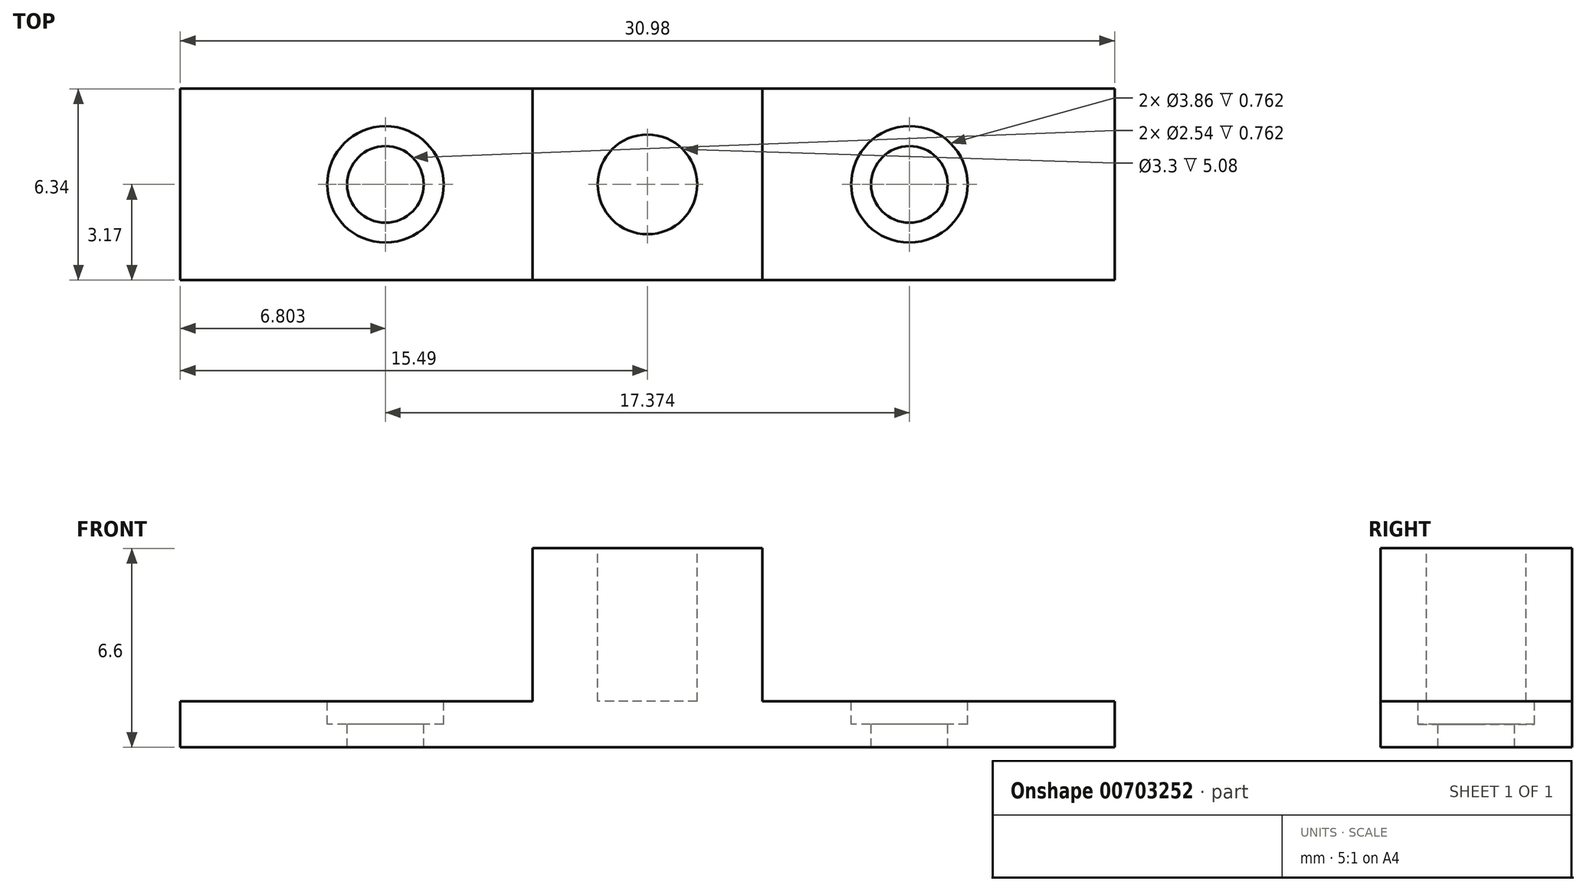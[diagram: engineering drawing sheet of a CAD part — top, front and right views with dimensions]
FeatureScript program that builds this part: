
annotation { "Feature Type Name" : "Feature", "Feature Type Description" : "" }
export const myFeature = defineFeature(function(context is Context, id is Id, definition is map)
    precondition{}
    {
        {
            var Q0;
            Q0=qCreatedBy(makeId("Top.planeOp"),FACE);
            var sketch = newSketch(context, id + "F0", { "sketchPlane" : qUnion([Q0])});
            skLineSegment(sketch, "E0", {"start": v(-15.5, 3.17) * mm, "end": v(15.5, 3.17) * mm});
            skLineSegment(sketch, "E1", {"start": v(15.5, 3.17) * mm, "end": v(15.5, -3.17) * mm});
            skLineSegment(sketch, "E2", {"start": v(15.5, -3.17) * mm, "end": v(-15.5, -3.18) * mm});
            skLineSegment(sketch, "E3", {"start": v(-15.5, -3.18) * mm, "end": v(-15.5, 3.17) * mm});
            skSolve(sketch);
        }
        {
            var Q0;
            Q0=makeQuery(id+"F0.imprint","IMPRINT",FACE,{"disambiguationData":[TD([[makeQuery(id+"F0.imprint","IMPRINT",EDGE,{"derivedFrom":sQuery(id+"F0.wireOp",EDGE,"E0")}),-1.0]])]});
            extrude(context, id + "F1", {"entities" : qUnion([Q0]), "depth" : 1.52 * mm, "offsetDistance" : 25.4 * mm});
        }
        {
            var Q0;
            Q0=makeQuery(id+"F1.opExtrude","CAP_FACE",FACE,{"disambiguationData":[OSD([sQuery(id+"F0.wireOp",EDGE,"E0"),sQuery(id+"F0.wireOp",EDGE,"E1"),sQuery(id+"F0.wireOp",EDGE,"E2"),sQuery(id+"F0.wireOp",EDGE,"E3")])],"isStart":false});
            var sketch = newSketch(context, id + "F2", { "sketchPlane" : qUnion([Q0])});
            skCircle(sketch, "E4", {"center": v(-8.69, 0) * mm, "radius": 1.93 * mm});
            skCircle(sketch, "E5", {"center": v(8.69, 0) * mm, "radius": 1.93 * mm});
            skSolve(sketch);
        }
        {
            var Q0;
            Q0 = qSketchRegion(id + "F2", true);
            extrude(context, id + "F3", {"entities" : qUnion([Q0]), "operationType" : NewBodyOperationType.REMOVE, "oppositeDirection" : true, "depth" : 0.76 * mm, "offsetDistance" : 25.4 * mm});
        }
        {
            var Q0;
            Q0=makeQuery(id+"F3.boolean.opBoolean","COPY",FACE,{"derivedFrom":makeQuery(id+"F3.opExtrude","CAP_FACE",FACE,{"disambiguationData":[OSD([sQuery(id+"F2.wireOp",EDGE,"E4")])],"isStart":false})});
            var sketch = newSketch(context, id + "F4", { "sketchPlane" : qUnion([Q0])});
            skCircle(sketch, "E6", {"center": v(-8.69, 0) * mm, "radius": 1.27 * mm});
            skCircle(sketch, "E7", {"center": v(8.69, 0) * mm, "radius": 1.27 * mm});
            skSolve(sketch);
        }
        {
            var Q0;
            Q0 = qSketchRegion(id + "F4", true);
            extrude(context, id + "F5", {"entities" : qUnion([Q0]), "operationType" : NewBodyOperationType.REMOVE, "oppositeDirection" : true, "depth" : 0.76 * mm, "offsetDistance" : 25.4 * mm});
        }
        {
            var Q0;
            Q0=makeQuery(id+"F1.opExtrude","CAP_FACE",FACE,{"disambiguationData":[OSD([sQuery(id+"F0.wireOp",EDGE,"E0"),sQuery(id+"F0.wireOp",EDGE,"E1"),sQuery(id+"F0.wireOp",EDGE,"E2"),sQuery(id+"F0.wireOp",EDGE,"E3")])],"isStart":false});
            var sketch = newSketch(context, id + "F6", { "sketchPlane" : qUnion([Q0])});
            skLineSegment(sketch, "E8.bottom", {"start": v(-3.8, -3.18) * mm, "end": v(3.81, -3.18) * mm});
            skLineSegment(sketch, "E8.top", {"start": v(-3.81, 3.17) * mm, "end": v(3.8, 3.17) * mm});
            skLineSegment(sketch, "E8.left", {"start": v(-3.8, -3.18) * mm, "end": v(-3.81, 3.17) * mm});
            skLineSegment(sketch, "E8.right", {"start": v(3.81, -3.18) * mm, "end": v(3.8, 3.17) * mm});
            skSolve(sketch);
        }
        {
            var Q0;
            Q0=makeQuery(id+"F6.imprint","IMPRINT",FACE,{"disambiguationData":[TD([[makeQuery(id+"F6.imprint","IMPRINT",EDGE,{"derivedFrom":sQuery(id+"F6.wireOp",EDGE,"E8.bottom")}),-1.0]])]});
            extrude(context, id + "F7", {"entities" : qUnion([Q0]), "operationType" : NewBodyOperationType.ADD, "depth" : 5.08 * mm, "offsetDistance" : 25.4 * mm});
        }
        {
            var Q0;
            Q0=makeQuery(id+"F7.opExtrude","CAP_FACE",FACE,{"disambiguationData":[OSD([sQuery(id+"F6.wireOp",EDGE,"E8.bottom"),sQuery(id+"F6.wireOp",EDGE,"E8.top"),sQuery(id+"F6.wireOp",EDGE,"E8.left"),sQuery(id+"F6.wireOp",EDGE,"E8.right")])],"isStart":false});
            var sketch = newSketch(context, id + "F8", { "sketchPlane" : qUnion([Q0])});
            skCircle(sketch, "E9", {"center": v(0, 0) * mm, "radius": 1.65 * mm});
            skSolve(sketch);
        }
        {
            var Q0;
            Q0=makeQuery(id+"F8.imprint","IMPRINT",FACE,{"disambiguationData":[TD([[makeQuery(id+"F8.imprint","IMPRINT",EDGE,{"derivedFrom":sQuery(id+"F8.wireOp",EDGE,"E9")}),1.0]])]});
            extrude(context, id + "F9", {"entities" : qUnion([Q0]), "operationType" : NewBodyOperationType.REMOVE, "oppositeDirection" : true, "depth" : 5.08 * mm, "offsetDistance" : 25.4 * mm});
        }
    });
